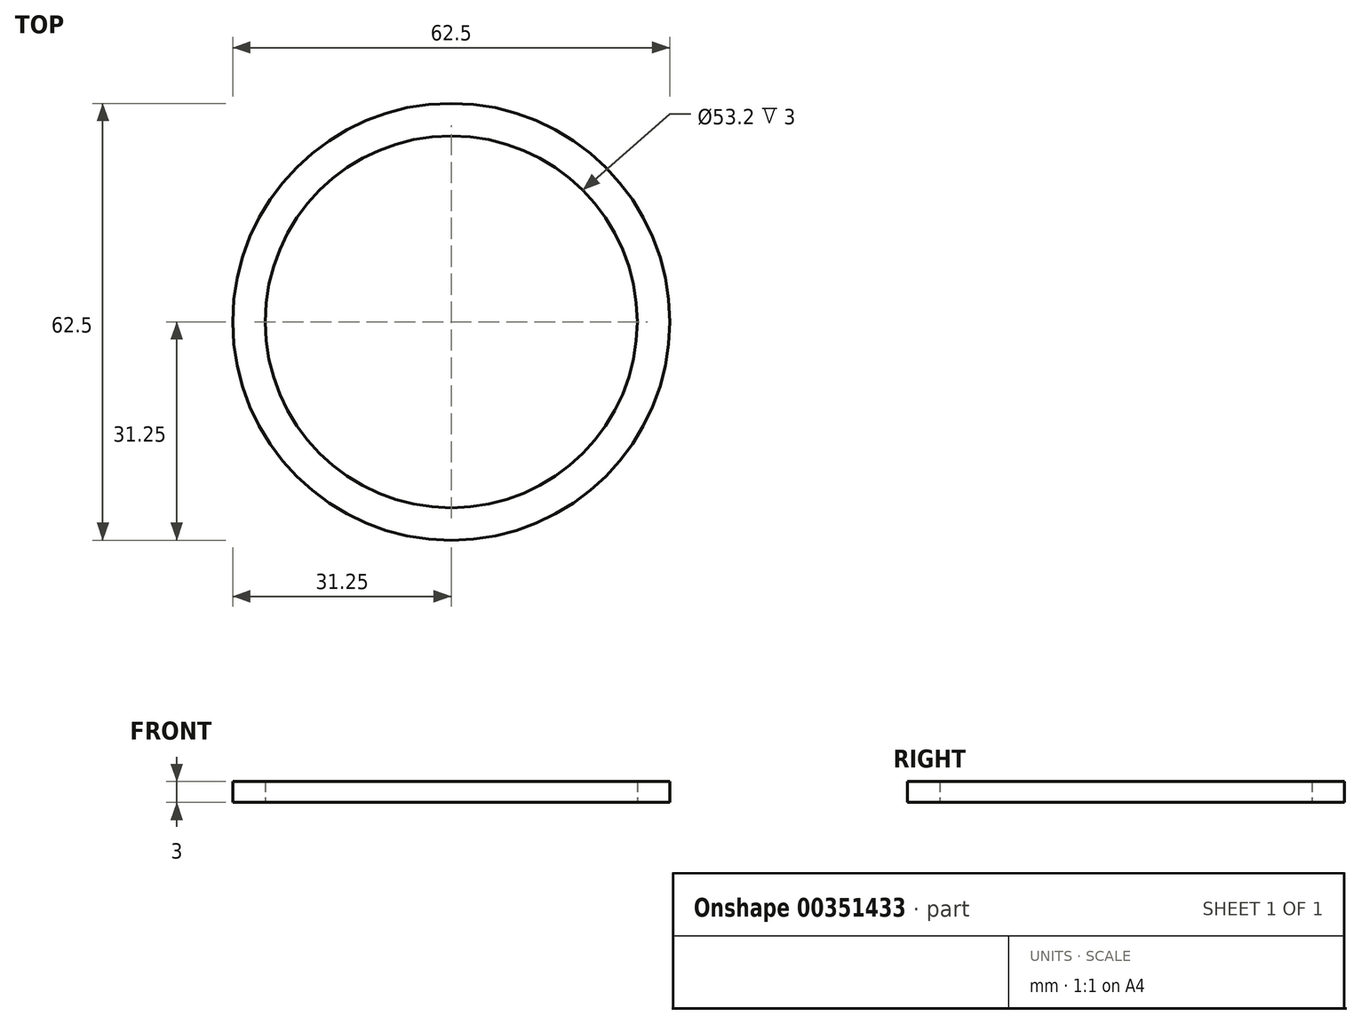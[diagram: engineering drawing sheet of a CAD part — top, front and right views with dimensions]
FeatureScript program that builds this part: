
annotation { "Feature Type Name" : "Feature", "Feature Type Description" : "" }
export const myFeature = defineFeature(function(context is Context, id is Id, definition is map)
    precondition{}
    {
        {
            var Q0;
            Q0=qCreatedBy(makeId("Top.planeOp"),FACE);
            var sketch = newSketch(context, id + "F0", { "sketchPlane" : qUnion([Q0])});
            skCircle(sketch, "E0", {"center": v(0, 0) * mm, "radius": 31.25 * mm});
            skCircle(sketch, "E1", {"center": v(0, 0) * mm, "radius": 26.6 * mm});
            skSolve(sketch);
        }
        {
            var Q0;
            Q0=makeQuery(id+"F0.imprint","IMPRINT",FACE,{"disambiguationData":[TD([[makeQuery(id+"F0.imprint","IMPRINT",EDGE,{"derivedFrom":sQuery(id+"F0.wireOp",EDGE,"E0")}),1.0]])]});
            extrude(context, id + "F1", {"entities" : qUnion([Q0]), "depth" : 3 * mm});
        }
    });
